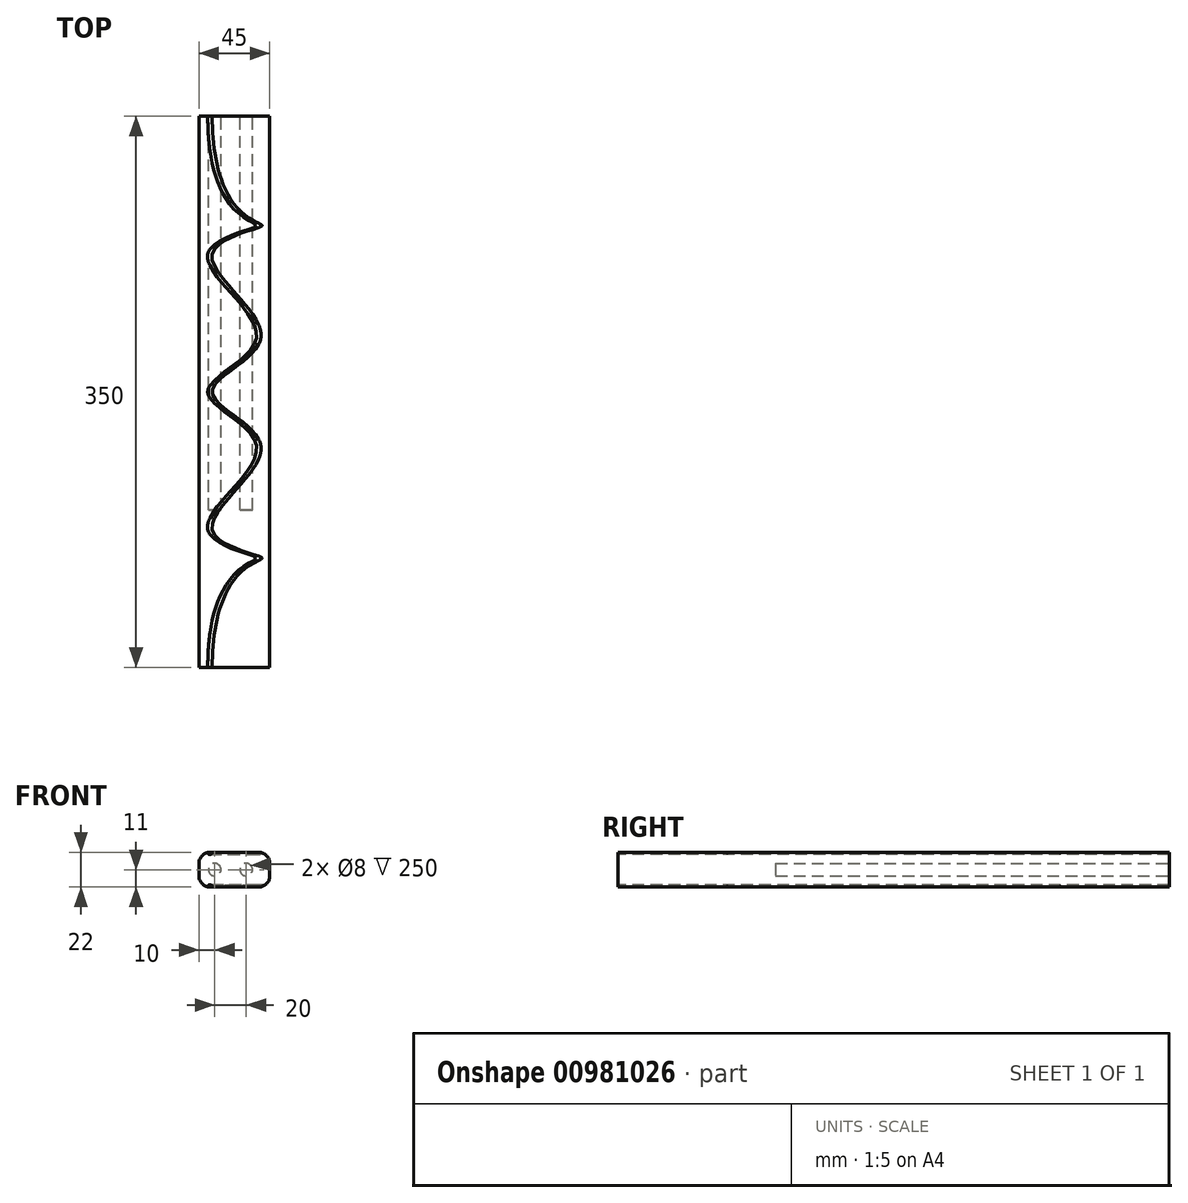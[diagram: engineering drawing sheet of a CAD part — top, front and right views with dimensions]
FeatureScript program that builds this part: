
annotation { "Feature Type Name" : "Feature", "Feature Type Description" : "" }
export const myFeature = defineFeature(function(context is Context, id is Id, definition is map)
    precondition{}
    {
        {
            var Q0;
            Q0=qCreatedBy(makeId("Top.planeOp"),FACE);
            var sketch = newSketch(context, id + "F0", { "sketchPlane" : qUnion([Q0])});
            skLineSegment(sketch, "E0.bottom", {"start": v(0, -45.32) * mm, "end": v(45, -45.32) * mm});
            skLineSegment(sketch, "E0.top", {"start": v(0, -395.32) * mm, "end": v(45, -395.32) * mm});
            skLineSegment(sketch, "E0.left", {"start": v(0, -45.32) * mm, "end": v(0, -395.32) * mm});
            skLineSegment(sketch, "E0.right", {"start": v(45, -45.32) * mm, "end": v(45, -395.32) * mm});
            skSolve(sketch);
        }
        {
            var Q0;
            Q0=makeQuery(id+"F0.imprint","IMPRINT",FACE,{"disambiguationData":[TD([[makeQuery(id+"F0.imprint","IMPRINT",EDGE,{"derivedFrom":sQuery(id+"F0.wireOp",EDGE,"E0.bottom")}),-1.0]])]});
            extrude(context, id + "F1", {"entities" : qUnion([Q0]), "depth" : 22 * mm, "offsetDistance" : 25 * mm});
        }
        {
            var Q0;
            Q0=makeQuery(id+"F1.opExtrude","SWEPT_FACE",FACE,{"disambiguationData":[OSD([sQuery(id+"F0.wireOp",EDGE,"E0.bottom")])]});
            var sketch = newSketch(context, id + "F2", { "sketchPlane" : qUnion([Q0])});
            skCircle(sketch, "E1", {"center": v(-10, 11) * mm, "radius": 4 * mm});
            skLineSegment(sketch, "E2", {"start": v(0, 11) * mm, "end": v(-45, 11) * mm, "construction": true});
            skCircle(sketch, "E3", {"center": v(-30, 11) * mm, "radius": 4 * mm});
            skSolve(sketch);
        }
        {
            var Q0;
            Q0=makeQuery(id+"F2.imprint","IMPRINT",FACE,{"disambiguationData":[TD([[makeQuery(id+"F2.imprint","IMPRINT",EDGE,{"derivedFrom":sQuery(id+"F2.wireOp",EDGE,"E1")}),1.0]])]});
            var Q1;
            Q1=makeQuery(id+"F2.imprint","IMPRINT",FACE,{"disambiguationData":[TD([[makeQuery(id+"F2.imprint","IMPRINT",EDGE,{"derivedFrom":sQuery(id+"F2.wireOp",EDGE,"E3")}),1.0]])]});
            extrude(context, id + "F3", {"entities" : qUnion([Q0, Q1]), "operationType" : NewBodyOperationType.REMOVE, "oppositeDirection" : true, "depth" : 250 * mm, "offsetDistance" : 25 * mm});
        }
        {
            var Q0;
            Q0=makeQuery(id+"F1.opExtrude","CAP_EDGE",EDGE,{"disambiguationData":[OSD([sQuery(id+"F0.wireOp",EDGE,"E0.right")])],"isStart":true});
            var Q1;
            Q1=makeQuery(id+"F1.opExtrude","CAP_EDGE",EDGE,{"disambiguationData":[OSD([sQuery(id+"F0.wireOp",EDGE,"E0.left")])],"isStart":true});
            var Q2;
            Q2=makeQuery(id+"F1.opExtrude","CAP_EDGE",EDGE,{"disambiguationData":[OSD([sQuery(id+"F0.wireOp",EDGE,"E0.right")])],"isStart":false});
            var Q3;
            Q3=makeQuery(id+"F1.opExtrude","CAP_EDGE",EDGE,{"disambiguationData":[OSD([sQuery(id+"F0.wireOp",EDGE,"E0.left")])],"isStart":false});
            fillet(context, id + "F4", {"entities" : qUnion([Q0, Q1, Q2, Q3]), "radius" : 7 * mm, "tangentPropagation" : true, "allowEdgeOverflow" : false});
        }
        {
            var Q0;
            Q0=makeQuery(id+"F1.opExtrude","CAP_FACE",FACE,{"disambiguationData":[OSD([sQuery(id+"F0.wireOp",EDGE,"E0.bottom"),sQuery(id+"F0.wireOp",EDGE,"E0.top"),sQuery(id+"F0.wireOp",EDGE,"E0.left"),sQuery(id+"F0.wireOp",EDGE,"E0.right")])],"isStart":false});
            var sketch = newSketch(context, id + "F5", { "sketchPlane" : qUnion([Q0])});
            skFitSpline(sketch, "E4", {"points": [v(7, -395.32) * mm, v(38, -325.32) * mm, v(7, -307.82) * mm, v(38, -255.32) * mm, v(7, -220.32) * mm, v(38, -185.32) * mm, v(7, -132.82) * mm, v(38, -115.32) * mm, v(7, -45.32) * mm], "startDerivative": vector(0, 1409.43) * mm, "endDerivative": vector(0, 1409.43) * mm});
            skSolve(sketch);
        }
        {
            var Q0;
            Q0=makeQuery(id+"F1.opExtrude","SWEPT_FACE",FACE,{"disambiguationData":[OSD([sQuery(id+"F0.wireOp",EDGE,"E0.top")])]});
            var sketch = newSketch(context, id + "F6", { "sketchPlane" : qUnion([Q0])});
            skCircle(sketch, "E5", {"center": v(7, 22) * mm, "radius": 1.42 * mm});
            skSolve(sketch);
        }
        {
            var Q0;
            {var subQ0=sQuery(id+"F6.wireOp",EDGE,"E5");var subQ1=sQuery(id+"F0.wireOp",EDGE,"E0.top");var subQ2=makeQuery(id+"F1.opExtrude","CAP_EDGE",EDGE,{"disambiguationData":[OSD([subQ1])],"isStart":false});var subQ3=makeQuery(id+"F6.imprint","INTERSECT",VERTEX,{"derivedFrom":[subQ2,subQ0]});Q0=makeQuery(id+"F6.imprint","IMPRINT",FACE,{"disambiguationData":[TD([[makeQuery(id+"F6.imprint","IMPRINT",EDGE,{"disambiguationData":[TD([[subQ3,1.0]])],"derivedFrom":subQ0}),1.0]])]});}
            var Q1;
            {var subQ0=sQuery(id+"F6.wireOp",EDGE,"E5");var subQ1=sQuery(id+"F0.wireOp",EDGE,"E0.top");var subQ2=makeQuery(id+"F1.opExtrude","CAP_EDGE",EDGE,{"disambiguationData":[OSD([subQ1])],"isStart":false});var subQ3=makeQuery(id+"F6.imprint","INTERSECT",VERTEX,{"derivedFrom":[subQ2,subQ0]});Q1=makeQuery(id+"F6.imprint","IMPRINT",FACE,{"disambiguationData":[TD([[makeQuery(id+"F6.imprint","IMPRINT",EDGE,{"disambiguationData":[TD([[subQ3,-1.0]])],"derivedFrom":subQ0}),1.0]])]});}
            var Q2;
            Q2=sQuery(id+"F5.wireOp",EDGE,"E4");
            sweep(context, id + "F7", {"operationType" : NewBodyOperationType.REMOVE, "profiles" : qUnion([Q0, Q1]), "path" : qUnion([Q2]), "keepProfileOrientation" : true});
        }
        {
            var Q0;
            Q0=makeQuery(id+"F1.opExtrude","SWEPT_FACE",FACE,{"disambiguationData":[OSD([sQuery(id+"F0.wireOp",EDGE,"E0.bottom")])]});
            var sketch = newSketch(context, id + "F8", { "sketchPlane" : qUnion([Q0])});
            skLineSegment(sketch, "E6", {"start": v(-45.06, 11) * mm, "end": v(0, 11) * mm});
            skSolve(sketch);
        }
        {
            var Q0;
            {var subQ2=sQuery(id+"F0.wireOp",EDGE,"E0.bottom");Q0=makeQuery(id+"F8.imprint","IMPRINT",FACE,{"disambiguationData":[TD([[makeQuery(id+"F8.imprint","IMPRINT",EDGE,{"derivedFrom":makeQuery(id+"F1.opExtrude","CAP_EDGE",EDGE,{"disambiguationData":[OSD([subQ2])],"isStart":true})}),-1.0]])]});}
            var Q1;
            {var subQ0=sQuery(id+"F8.wireOp",EDGE,"E6");var subQ1=makeQuery(id+"F3.boolean.opBoolean","COPY",EDGE,{"derivedFrom":makeQuery(id+"F3.opExtrude","CAP_EDGE",EDGE,{"disambiguationData":[OSD([sQuery(id+"F2.wireOp",EDGE,"E3")])],"isStart":true})});var subQ2=makeQuery(id+"F8.imprint","INTERSECT",VERTEX,{"disambiguationData":[OD(0.0)],"derivedFrom":[subQ1,subQ0]});Q1=makeQuery(id+"F8.imprint","IMPRINT",FACE,{"disambiguationData":[TD([[makeQuery(id+"F8.imprint","IMPRINT",EDGE,{"disambiguationData":[TD([[subQ2,-1.0]])],"derivedFrom":subQ0}),-1.0]])]});}
            var Q2;
            {var subQ0=sQuery(id+"F8.wireOp",EDGE,"E6");var subQ1=makeQuery(id+"F3.boolean.opBoolean","COPY",EDGE,{"derivedFrom":makeQuery(id+"F3.opExtrude","CAP_EDGE",EDGE,{"disambiguationData":[OSD([sQuery(id+"F2.wireOp",EDGE,"E1")])],"isStart":true})});var subQ2=makeQuery(id+"F8.imprint","INTERSECT",VERTEX,{"disambiguationData":[OD(0.0)],"derivedFrom":[subQ1,subQ0]});Q2=makeQuery(id+"F8.imprint","IMPRINT",FACE,{"disambiguationData":[TD([[makeQuery(id+"F8.imprint","IMPRINT",EDGE,{"disambiguationData":[TD([[subQ2,-1.0]])],"derivedFrom":subQ0}),-1.0]])]});}
            var Q3;
            Q3=makeQuery(id+"F1.opExtrude","SWEPT_FACE",FACE,{"disambiguationData":[OSD([sQuery(id+"F0.wireOp",EDGE,"E0.top")])]});
            extrude(context, id + "F9", {"entities" : qUnion([Q0, Q1, Q2]), "operationType" : NewBodyOperationType.REMOVE, "endBound" : BoundingType.UP_TO_SURFACE, "oppositeDirection" : true, "depth" : 25 * mm, "endBoundEntityFace" : qUnion([Q3]), "offsetDistance" : 25 * mm});
        }
        {
            var Q0;
            Q0=makeQuery(id+"F1.opExtrude","SWEPT_BODY",BODY,{"disambiguationData":[OSD([sQuery(id+"F0.wireOp",EDGE,"E0.bottom"),sQuery(id+"F0.wireOp",EDGE,"E0.top"),sQuery(id+"F0.wireOp",EDGE,"E0.left"),sQuery(id+"F0.wireOp",EDGE,"E0.right")])]});
            var Q1;
            Q1=makeQuery(id+"F9.boolean.opBoolean","COPY",FACE,{"derivedFrom":makeQuery(id+"F9.opExtrude","SWEPT_FACE",FACE,{"disambiguationData":[OSD([sQuery(id+"F8.wireOp",EDGE,"E6")])]})});
            mirror(context, id + "F10", {"operationType" : NewBodyOperationType.ADD, "entities" : qUnion([Q0]), "mirrorPlane" : qUnion([Q1])});
        }
    });
